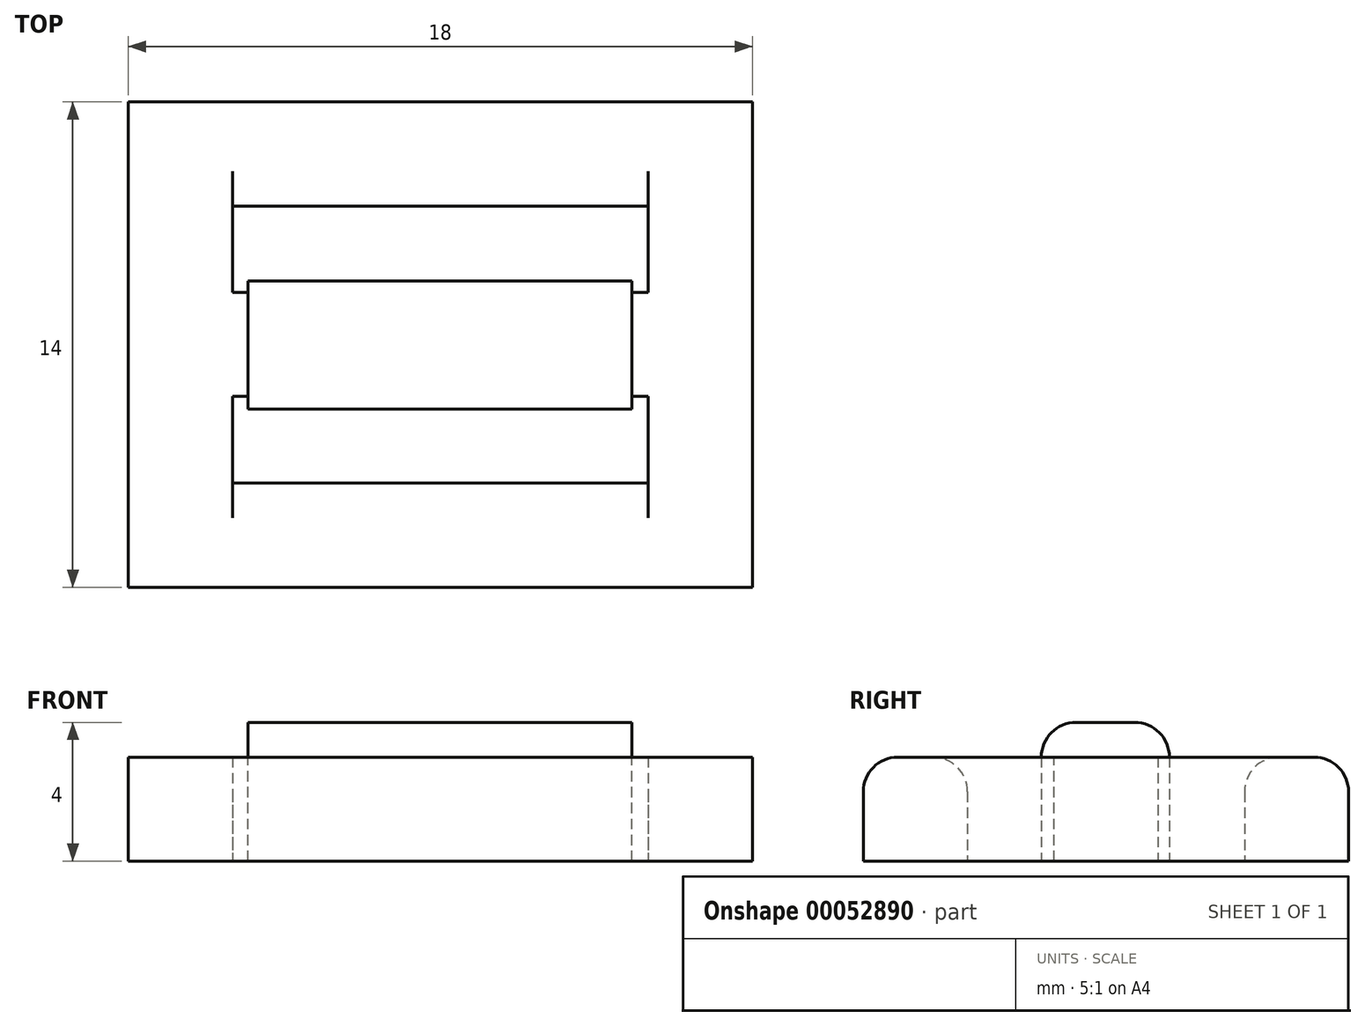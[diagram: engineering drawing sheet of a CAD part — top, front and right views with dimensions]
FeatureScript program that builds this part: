
annotation { "Feature Type Name" : "Feature", "Feature Type Description" : "" }
export const myFeature = defineFeature(function(context is Context, id is Id, definition is map)
    precondition{}
    {
        {
            var Q0;
            Q0=qCreatedBy(makeId("Top.planeOp"),FACE);
            var sketch = newSketch(context, id + "F0", { "sketchPlane" : qUnion([Q0])});
            skLineSegment(sketch, "E0.bottom", {"start": v(0, 0) * mm, "end": v(18, 0) * mm});
            skLineSegment(sketch, "E0.top", {"start": v(0, -14) * mm, "end": v(18, -14) * mm});
            skLineSegment(sketch, "E0.left", {"start": v(0, 0) * mm, "end": v(0, -14) * mm});
            skLineSegment(sketch, "E0.right", {"start": v(18, 0) * mm, "end": v(18, -14) * mm});
            skSolve(sketch);
        }
        {
            var Q0;
            Q0=makeQuery(id+"F0.imprint","IMPRINT",FACE,{"disambiguationData":[TD([[makeQuery(id+"F0.imprint","IMPRINT",EDGE,{"derivedFrom":sQuery(id+"F0.wireOp",EDGE,"E0.bottom")}),-1.0]])]});
            var sketch = newSketch(context, id + "F1", { "sketchPlane" : qUnion([Q0])});
            skLineSegment(sketch, "E1.bottom", {"start": v(3, -3) * mm, "end": v(15, -3) * mm});
            skLineSegment(sketch, "E1.top", {"start": v(3, -5.5) * mm, "end": v(15, -5.5) * mm});
            skLineSegment(sketch, "E1.left", {"start": v(3, -3) * mm, "end": v(3, -5.5) * mm});
            skLineSegment(sketch, "E1.right", {"start": v(15, -3) * mm, "end": v(15, -5.5) * mm});
            skLineSegment(sketch, "E2.bottom", {"start": v(15, -11) * mm, "end": v(3, -11) * mm});
            skLineSegment(sketch, "E2.top", {"start": v(15, -8.5) * mm, "end": v(3, -8.5) * mm});
            skLineSegment(sketch, "E2.left", {"start": v(15, -11) * mm, "end": v(15, -8.5) * mm});
            skLineSegment(sketch, "E2.right", {"start": v(3, -11) * mm, "end": v(3, -8.5) * mm});
            skSolve(sketch);
        }
        {
            var Q0;
            Q0=makeQuery(id+"F0.imprint","IMPRINT",FACE,{"disambiguationData":[TD([[makeQuery(id+"F0.imprint","IMPRINT",EDGE,{"derivedFrom":sQuery(id+"F0.wireOp",EDGE,"E0.bottom")}),-1.0]])]});
            var sketch = newSketch(context, id + "F2", { "sketchPlane" : qUnion([Q0])});
            skLineSegment(sketch, "E3.bottom", {"start": v(3.45, -5.17) * mm, "end": v(14.53, -5.17) * mm});
            skLineSegment(sketch, "E3.top", {"start": v(3.45, -8.86) * mm, "end": v(14.53, -8.86) * mm});
            skLineSegment(sketch, "E3.left", {"start": v(3.45, -5.17) * mm, "end": v(3.45, -8.86) * mm});
            skLineSegment(sketch, "E3.right", {"start": v(14.53, -5.17) * mm, "end": v(14.53, -8.86) * mm});
            skSolve(sketch);
        }
        {
            var Q0;
            Q0=makeQuery(id+"F0.imprint","IMPRINT",FACE,{"disambiguationData":[TD([[makeQuery(id+"F0.imprint","IMPRINT",EDGE,{"derivedFrom":sQuery(id+"F0.wireOp",EDGE,"E0.bottom")}),-1.0]])]});
            extrude(context, id + "F3", {"entities" : qUnion([Q0]), "depth" : 3 * mm});
        }
        {
            var Q0;
            Q0 = qSketchRegion(id + "F1", true);
            extrude(context, id + "F4", {"entities" : qUnion([Q0]), "operationType" : NewBodyOperationType.REMOVE, "depth" : 25 * mm});
        }
        {
            var Q0;
            Q0 = qSketchRegion(id + "F2", true);
            extrude(context, id + "F5", {"entities" : qUnion([Q0]), "operationType" : NewBodyOperationType.ADD, "depth" : 4 * mm});
        }
        {
            var Q0;
            Q0=makeQuery(id+"F5.opExtrude","CAP_EDGE",EDGE,{"disambiguationData":[OSD([sQuery(id+"F2.wireOp",EDGE,"E3.top")])],"isStart":false});
            var Q1;
            Q1=makeQuery(id+"F5.opExtrude","CAP_EDGE",EDGE,{"disambiguationData":[OSD([sQuery(id+"F2.wireOp",EDGE,"E3.bottom")])],"isStart":false});
            var Q2;
            Q2=makeQuery(id+"F4.boolean.opBoolean","INTERSECT",EDGE,{"derivedFrom":[makeQuery(id+"F3.opExtrude","CAP_FACE",FACE,{"disambiguationData":[OSD([sQuery(id+"F0.wireOp",EDGE,"E0.bottom"),sQuery(id+"F0.wireOp",EDGE,"E0.top"),sQuery(id+"F0.wireOp",EDGE,"E0.left"),sQuery(id+"F0.wireOp",EDGE,"E0.right")])],"isStart":false}),makeQuery(id+"F4.opExtrude","SWEPT_FACE",FACE,{"disambiguationData":[OSD([sQuery(id+"F1.wireOp",EDGE,"E1.bottom")])]})]});
            var Q3;
            Q3=makeQuery(id+"F4.boolean.opBoolean","INTERSECT",EDGE,{"derivedFrom":[makeQuery(id+"F3.opExtrude","CAP_FACE",FACE,{"disambiguationData":[OSD([sQuery(id+"F0.wireOp",EDGE,"E0.bottom"),sQuery(id+"F0.wireOp",EDGE,"E0.top"),sQuery(id+"F0.wireOp",EDGE,"E0.left"),sQuery(id+"F0.wireOp",EDGE,"E0.right")])],"isStart":false}),makeQuery(id+"F4.opExtrude","SWEPT_FACE",FACE,{"disambiguationData":[OSD([sQuery(id+"F1.wireOp",EDGE,"E2.bottom")])]})]});
            var Q4;
            Q4=makeQuery(id+"F3.opExtrude","CAP_EDGE",EDGE,{"disambiguationData":[OSD([sQuery(id+"F0.wireOp",EDGE,"E0.top")])],"isStart":false});
            var Q5;
            Q5=makeQuery(id+"F3.opExtrude","CAP_EDGE",EDGE,{"disambiguationData":[OSD([sQuery(id+"F0.wireOp",EDGE,"E0.bottom")])],"isStart":false});
            fillet(context, id + "F6", {"entities" : qUnion([Q0, Q1, Q2, Q3, Q4, Q5]), "radius" : 1 * mm, "tangentPropagation" : true, "allowEdgeOverflow" : false});
        }
    });
